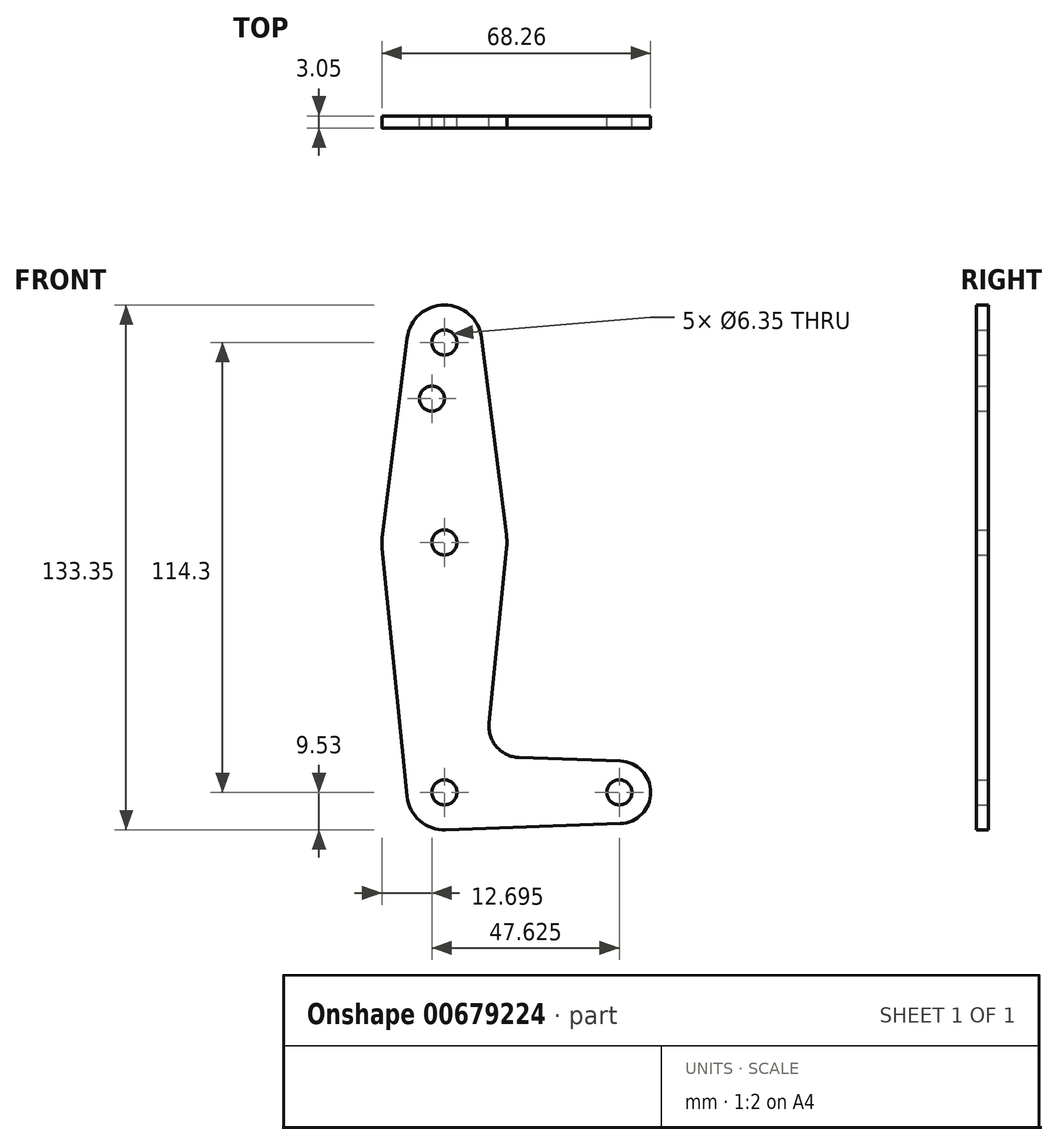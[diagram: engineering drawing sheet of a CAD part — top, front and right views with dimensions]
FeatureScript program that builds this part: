
annotation { "Feature Type Name" : "Feature", "Feature Type Description" : "" }
export const myFeature = defineFeature(function(context is Context, id is Id, definition is map)
    precondition{}
    {
        {
            var Q0;
            Q0=qCreatedBy(makeId("Front.planeOp"),FACE);
            var sketch = newSketch(context, id + "F0", { "sketchPlane" : qUnion([Q0])});
            skCircle(sketch, "E0", {"center": v(0, 0) * mm, "radius": 15.88 * mm});
            skCircle(sketch, "E1", {"center": v(0, 50.8) * mm, "radius": 9.53 * mm});
            skCircle(sketch, "E2", {"center": v(0, -63.5) * mm, "radius": 9.53 * mm});
            skCircle(sketch, "E3", {"center": v(44.45, -63.5) * mm, "radius": 7.94 * mm});
            skLineSegment(sketch, "E4", {"start": v(0, 0) * mm, "end": v(0, -63.5) * mm, "construction": true});
            skLineSegment(sketch, "E5", {"start": v(0, 0) * mm, "end": v(0, 50.8) * mm, "construction": true});
            skLineSegment(sketch, "E6", {"start": v(0, -63.5) * mm, "end": v(44.45, -63.5) * mm, "construction": true});
            skLineSegment(sketch, "E7", {"start": v(-9.45, 52) * mm, "end": v(-15.75, 1.98) * mm});
            skLineSegment(sketch, "E8", {"start": v(-9.48, -64.45) * mm, "end": v(-15.8, -1.59) * mm});
            skLineSegment(sketch, "E9", {"start": v(0.34, -73.02) * mm, "end": v(44.73, -71.43) * mm});
            skLineSegment(sketch, "E10", {"start": v(44.73, -55.57) * mm, "end": v(18.97, -54.65) * mm});
            skLineSegment(sketch, "E11", {"start": v(9.45, 52) * mm, "end": v(15.75, 1.98) * mm});
            skLineSegment(sketch, "E12", {"start": v(15.8, -1.59) * mm, "end": v(11.34, -45.9) * mm});
            skLineSegment(sketch, "E13", {"start": v(0, 0) * mm, "end": v(-3.17, 0) * mm, "construction": true});
            skCircle(sketch, "E14", {"center": v(0, 50.8) * mm, "radius": 3.18 * mm});
            skCircle(sketch, "E15", {"center": v(-3.18, 36.53) * mm, "radius": 3.18 * mm});
            skCircle(sketch, "E16", {"center": v(0, 0) * mm, "radius": 3.18 * mm});
            skCircle(sketch, "E17", {"center": v(0, -63.5) * mm, "radius": 3.18 * mm});
            skCircle(sketch, "E18", {"center": v(44.45, -63.5) * mm, "radius": 3.18 * mm});
            skArc(sketch, "E19", {"start": v(11.34, -45.9) * mm, "mid": v(13.26, -51.93) * mm, "end": v(18.97, -54.65) * mm});
            skSolve(sketch);
        }
        {
            var Q0;
            Q0=makeQuery(id+"F0.imprint","IMPRINT",FACE,{"disambiguationData":[TD([[makeQuery(id+"F0.imprint","IMPRINT",EDGE,{"derivedFrom":sQuery(id+"F0.wireOp",EDGE,"E14")}),-1.0]])]});
            var Q1;
            Q1=makeQuery(id+"F0.imprint","IMPRINT",FACE,{"disambiguationData":[TD([[makeQuery(id+"F0.imprint","IMPRINT",EDGE,{"derivedFrom":sQuery(id+"F0.wireOp",EDGE,"E17")}),-1.0]])]});
            var Q2;
            Q2=makeQuery(id+"F0.imprint","IMPRINT",FACE,{"disambiguationData":[TD([[makeQuery(id+"F0.imprint","IMPRINT",EDGE,{"derivedFrom":sQuery(id+"F0.wireOp",EDGE,"E18")}),-1.0]])]});
            var Q3;
            Q3=makeQuery(id+"F0.imprint","IMPRINT",FACE,{"disambiguationData":[TD([[makeQuery(id+"F0.imprint","IMPRINT",EDGE,{"derivedFrom":sQuery(id+"F0.wireOp",EDGE,"E16")}),-1.0]])]});
            var Q4;
            {var subQ0=sQuery(id+"F0.wireOp",EDGE,"E7");Q4=makeQuery(id+"F0.imprint","IMPRINT",FACE,{"disambiguationData":[TD([[makeQuery(id+"F0.imprint","IMPRINT",EDGE,{"derivedFrom":subQ0}),1.0]])]});}
            var Q5;
            {var subQ3=sQuery(id+"F0.wireOp",EDGE,"E8");Q5=makeQuery(id+"F0.imprint","IMPRINT",FACE,{"disambiguationData":[TD([[makeQuery(id+"F0.imprint","IMPRINT",EDGE,{"derivedFrom":subQ3}),-1.0]])]});}
            extrude(context, id + "F1", {"entities" : qUnion([Q0, Q1, Q2, Q3, Q4, Q5]), "depth" : 3.05 * mm, "offsetDistance" : 25.4 * mm});
        }
    });
